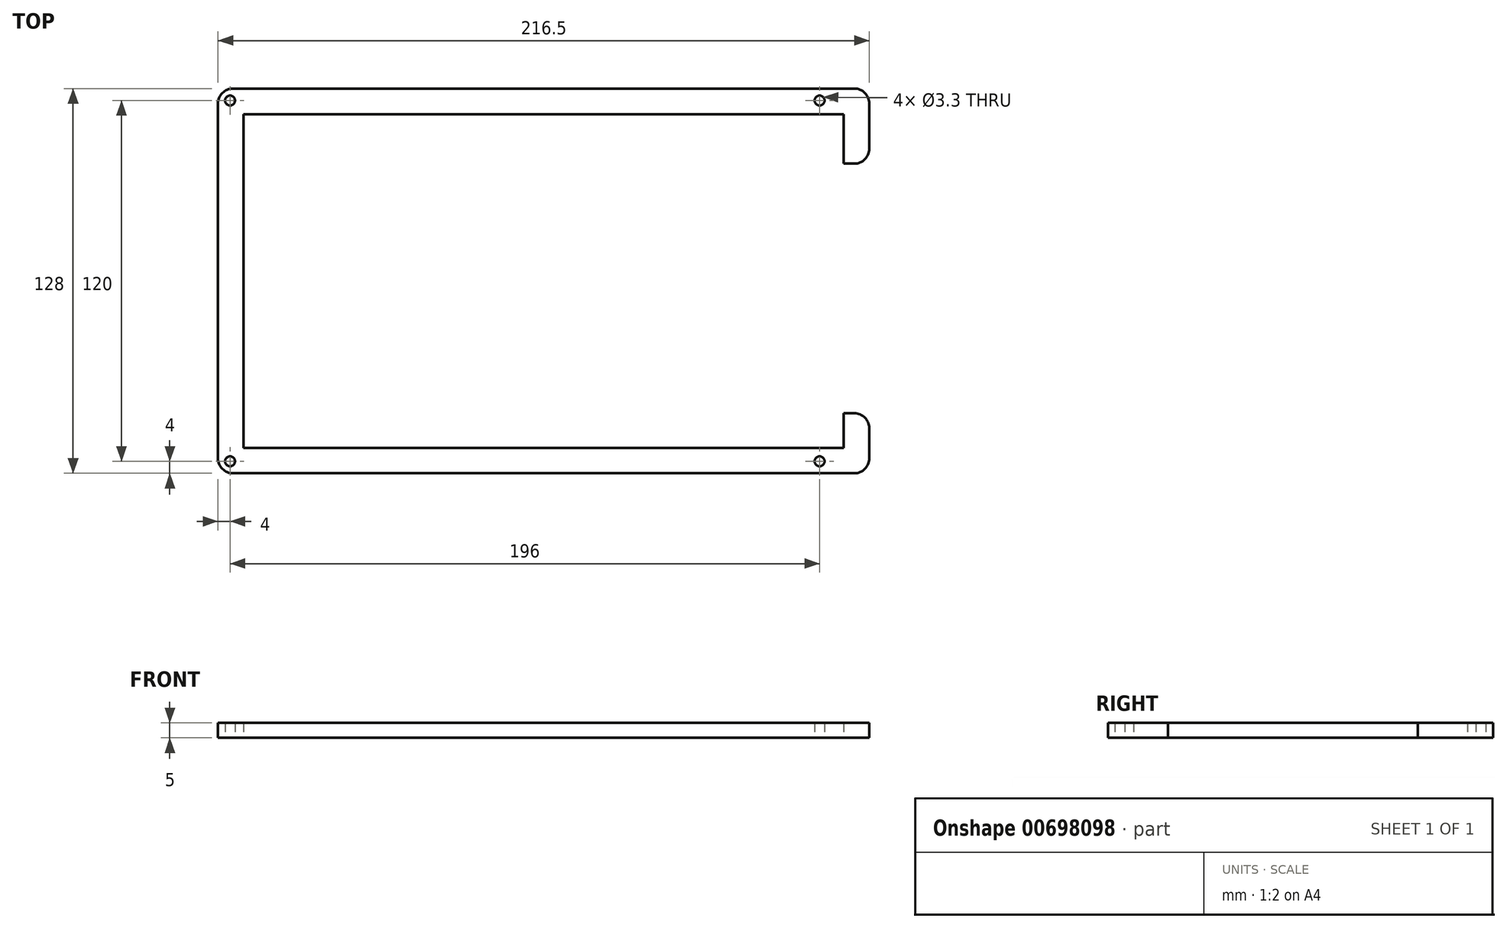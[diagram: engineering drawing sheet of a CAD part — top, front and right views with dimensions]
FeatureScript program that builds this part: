
annotation { "Feature Type Name" : "Feature", "Feature Type Description" : "" }
export const myFeature = defineFeature(function(context is Context, id is Id, definition is map)
    precondition{}
    {
        {
            var Q0;
            Q0=qCreatedBy(makeId("Top.planeOp"),FACE);
            var sketch = newSketch(context, id + "F0", { "sketchPlane" : qUnion([Q0])});
            skLineSegment(sketch, "E0.bottom", {"start": v(83, 50.5) * mm, "end": v(-83, 50.5) * mm});
            skLineSegment(sketch, "E0.top", {"start": v(83, -50.5) * mm, "end": v(-83, -50.5) * mm});
            skLineSegment(sketch, "E0.left", {"start": v(83, 50.5) * mm, "end": v(83, -50.5) * mm});
            skLineSegment(sketch, "E0.right", {"start": v(-83, 50.5) * mm, "end": v(-83, -50.5) * mm});
            skPoint(sketch, "E0.middle", {"position": v(0, 0) * mm});
            skLineSegment(sketch, "E1.0", {"start": v(-91, 54.5) * mm, "end": v(-91, -53.5) * mm, "construction": true});
            skLineSegment(sketch, "E1.1", {"start": v(93, 54.5) * mm, "end": v(-91, 54.5) * mm, "construction": true});
            skLineSegment(sketch, "E1.2", {"start": v(93, 54.5) * mm, "end": v(93, -53.5) * mm, "construction": true});
            skLineSegment(sketch, "E1.3", {"start": v(93, -53.5) * mm, "end": v(-91, -53.5) * mm, "construction": true});
            skLineSegment(sketch, "E2.0", {"start": v(103, 64.5) * mm, "end": v(-101, 64.5) * mm});
            skLineSegment(sketch, "E2.2", {"start": v(103, -63.5) * mm, "end": v(-101, -63.5) * mm});
            skLineSegment(sketch, "E2.3", {"start": v(-101, 64.5) * mm, "end": v(-101, -63.5) * mm});
            skLineSegment(sketch, "E3.0", {"start": v(99, 60.5) * mm, "end": v(-97, 60.5) * mm, "construction": true});
            skLineSegment(sketch, "E3.1", {"start": v(99, 60.5) * mm, "end": v(99, -59.5) * mm, "construction": true});
            skLineSegment(sketch, "E3.2", {"start": v(99, -59.5) * mm, "end": v(-97, -59.5) * mm, "construction": true});
            skLineSegment(sketch, "E3.3", {"start": v(-97, 60.5) * mm, "end": v(-97, -59.5) * mm, "construction": true});
            skLineSegment(sketch, "E4", {"start": v(103, 64.5) * mm, "end": v(115.5, 64.5) * mm});
            skLineSegment(sketch, "E5", {"start": v(115.5, -63.5) * mm, "end": v(103, -63.5) * mm});
            skLineSegment(sketch, "E6", {"start": v(115.5, 64.5) * mm, "end": v(115.5, 39.5) * mm});
            skPoint(sketch, "E7.orphan", {"position": v(133, -63.5) * mm});
            skLineSegment(sketch, "E8.0", {"start": v(103, 56) * mm, "end": v(107, 56) * mm});
            skLineSegment(sketch, "E8.1", {"start": v(-92.5, 56) * mm, "end": v(-92.5, -55) * mm});
            skLineSegment(sketch, "E8.2", {"start": v(103, -55) * mm, "end": v(-92.5, -55) * mm});
            skLineSegment(sketch, "E8.3", {"start": v(103, 56) * mm, "end": v(-92.5, 56) * mm});
            skLineSegment(sketch, "E8.4", {"start": v(107, -55) * mm, "end": v(103, -55) * mm});
            skLineSegment(sketch, "E8.5", {"start": v(107, 56) * mm, "end": v(107, 39.5) * mm});
            skLineSegment(sketch, "E9", {"start": v(107, 39.5) * mm, "end": v(115.5, 39.5) * mm});
            skLineSegment(sketch, "E10", {"start": v(107, -43.5) * mm, "end": v(115.5, -43.5) * mm});
            skLineSegment(sketch, "E11.trimOffspring", {"start": v(107, -43.5) * mm, "end": v(107, -55) * mm});
            skLineSegment(sketch, "E12.trimOffspring", {"start": v(115.5, -43.5) * mm, "end": v(115.5, -63.5) * mm});
            skSolve(sketch);
        }
        {
            var Q0;
            Q0=makeQuery(id+"F0.imprint","IMPRINT",FACE,{"disambiguationData":[TD([[makeQuery(id+"F0.imprint","IMPRINT",EDGE,{"derivedFrom":sQuery(id+"F0.wireOp",EDGE,"E2.0")}),1.0]])]});
            extrude(context, id + "F1", {"entities" : qUnion([Q0]), "depth" : 5 * mm, "offsetDistance" : 25 * mm});
        }
        {
            var Q0;
            Q0=sQuery(id+"F0.wireOp",VERTEX,"E3.0.end");
            var Q1;
            Q1=sQuery(id+"F0.wireOp",VERTEX,"E3.0.start");
            var Q2;
            Q2=sQuery(id+"F0.wireOp",VERTEX,"E3.1.end");
            var Q3;
            Q3=sQuery(id+"F0.wireOp",VERTEX,"E3.2.end");
            var Q4;
            Q4=makeQuery(id+"F1.opExtrude","SWEPT_BODY",BODY,{"disambiguationData":[OSD([sQuery(id+"F0.wireOp",EDGE,"E0.bottom"),sQuery(id+"F0.wireOp",EDGE,"E0.top"),sQuery(id+"F0.wireOp",EDGE,"E0.left"),sQuery(id+"F0.wireOp",EDGE,"E0.right"),sQuery(id+"F0.wireOp",EDGE,"E2.0"),sQuery(id+"F0.wireOp",EDGE,"E2.1"),sQuery(id+"F0.wireOp",EDGE,"E2.2"),sQuery(id+"F0.wireOp",EDGE,"E2.3")])]});
            hole(context, id + "F2", {"style" : HoleStyle.SIMPLE, "endStyle" : HoleEndStyle.THROUGH, "oppositeDirection" : true, "standardTappedOrClearance" : lookupTablePath({ "standard" : "ISO", "fit" : "Normal", "size" : "M3", "type" : "Clearance" }), "standardBlindInLast" : lookupTablePath({ "fit" : "Standard", "standard" : "ISO", "size" : "M3", "type" : "Clearance" }), "holeDiameter" : 3.3 * mm, "majorDiameter" : 5 * mm, "isTappedThrough" : true, "tappedDepth" : 12 * mm, "tapClearance" : 3, "startFromSketch" : true, "locations" : qUnion([Q0, Q1, Q2, Q3]), "scope" : qUnion([Q4])});
        }
        {
            var Q0;
            Q0=makeQuery(id+"F1.opExtrude","SWEPT_EDGE",EDGE,{"disambiguationData":[OSD([sQuery(id+"F0.wireOp",EDGE,"E2.2"),sQuery(id+"F0.wireOp",EDGE,"E2.3")])]});
            var Q1;
            Q1=makeQuery(id+"F1.opExtrude","SWEPT_EDGE",EDGE,{"disambiguationData":[OSD([sQuery(id+"F0.wireOp",EDGE,"E5"),sQuery(id+"F0.wireOp",EDGE,"E12.trimOffspring")])]});
            var Q2;
            Q2=makeQuery(id+"F1.opExtrude","SWEPT_EDGE",EDGE,{"disambiguationData":[OSD([sQuery(id+"F0.wireOp",EDGE,"E10"),sQuery(id+"F0.wireOp",EDGE,"E12.trimOffspring")])]});
            var Q3;
            Q3=makeQuery(id+"F1.opExtrude","SWEPT_EDGE",EDGE,{"disambiguationData":[OSD([sQuery(id+"F0.wireOp",EDGE,"E6"),sQuery(id+"F0.wireOp",EDGE,"E9")])]});
            var Q4;
            Q4=makeQuery(id+"F1.opExtrude","SWEPT_EDGE",EDGE,{"disambiguationData":[OSD([sQuery(id+"F0.wireOp",EDGE,"E4"),sQuery(id+"F0.wireOp",EDGE,"E6")])]});
            var Q5;
            Q5=makeQuery(id+"F1.opExtrude","SWEPT_EDGE",EDGE,{"disambiguationData":[OSD([sQuery(id+"F0.wireOp",EDGE,"E2.0"),sQuery(id+"F0.wireOp",EDGE,"E2.3")])]});
            fillet(context, id + "F3", {"entities" : qUnion([Q0, Q1, Q2, Q3, Q4, Q5]), "radius" : 5 * mm, "tangentPropagation" : true, "allowEdgeOverflow" : false});
        }
    });
